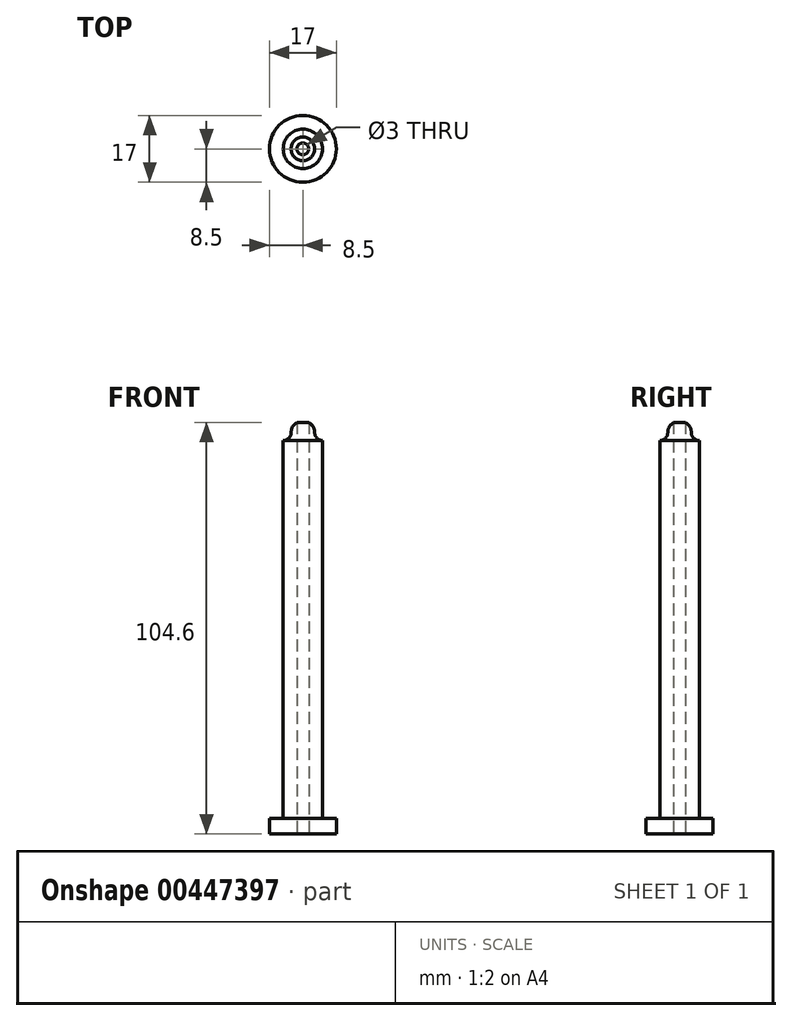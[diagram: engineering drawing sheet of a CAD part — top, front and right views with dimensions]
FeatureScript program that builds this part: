
annotation { "Feature Type Name" : "Feature", "Feature Type Description" : "" }
export const myFeature = defineFeature(function(context is Context, id is Id, definition is map)
    precondition{}
    {
        {
            var Q0;
            Q0=qCreatedBy(makeId("Top.planeOp"),FACE);
            var sketch = newSketch(context, id + "F0", { "sketchPlane" : qUnion([Q0])});
            skCircle(sketch, "E0", {"center": v(0, 0) * mm, "radius": 8.5 * mm});
            skSolve(sketch);
        }
        {
            var Q0;
            Q0=qSketchRegion(id+"F0",true);
            extrude(context, id + "F1", {"entities" : qUnion([Q0]), "depth" : 4 * mm});
        }
        {
            var Q0;
            Q0=qCreatedBy(makeId("Top.planeOp"),FACE);
            var sketch = newSketch(context, id + "F2", { "sketchPlane" : qUnion([Q0])});
            skCircle(sketch, "E1", {"center": v(0, 0) * mm, "radius": 5 * mm});
            skSolve(sketch);
        }
        {
            var Q0;
            Q0=qSketchRegion(id+"F2",true);
            extrude(context, id + "F3", {"entities" : qUnion([Q0]), "operationType" : NewBodyOperationType.ADD, "depth" : 100 * mm});
        }
        {
            var Q0;
            Q0=qCreatedBy(makeId("Right.planeOp"),FACE);
            var sketch = newSketch(context, id + "F4", { "sketchPlane" : qUnion([Q0])});
            skLineSegment(sketch, "E2", {"start": v(0, 102) * mm, "end": v(0, 100) * mm});
            skLineSegment(sketch, "E3", {"start": v(0, 100) * mm, "end": v(5, 100) * mm});
            skLineSegment(sketch, "E4", {"start": v(3, 102) * mm, "end": v(0, 102) * mm});
            skArc(sketch, "E5", {"start": v(3, 102) * mm, "mid": v(3.59, 100.59) * mm, "end": v(5, 100) * mm});
            skSolve(sketch);
        }
        {
            var Q0;
            Q0=makeQuery(id+"F4.imprint","IMPRINT",FACE,{"disambiguationData":[TD([[makeQuery(id+"F4.imprint","IMPRINT",EDGE,{"derivedFrom":sQuery(id+"F4.wireOp",EDGE,"E2")}),1.0]])]});
            var Q1;
            Q1=sQuery(id+"F4.wireOp",EDGE,"E2");
            revolve(context, id + "F5", {"operationType" : NewBodyOperationType.ADD, "entities" : qUnion([Q0]), "axis" : qUnion([Q1]), "revolveType" : RevolveType.FULL});
        }
        {
            var Q0;
            Q0=qCreatedBy(makeId("Right.planeOp"),FACE);
            var sketch = newSketch(context, id + "F6", { "sketchPlane" : qUnion([Q0])});
            skLineSegment(sketch, "E6", {"start": v(0, 102) * mm, "end": v(0, 105) * mm});
            skLineSegment(sketch, "E7", {"start": v(3, 102) * mm, "end": v(0, 102) * mm});
            skArc(sketch, "E8", {"start": v(3, 102) * mm, "mid": v(2.12, 104.12) * mm, "end": v(0, 105) * mm});
            skSolve(sketch);
        }
        {
            var Q0;
            Q0=makeQuery(id+"F6.imprint","IMPRINT",FACE,{"disambiguationData":[TD([[makeQuery(id+"F6.imprint","IMPRINT",EDGE,{"derivedFrom":sQuery(id+"F6.wireOp",EDGE,"E6")}),-1.0]])]});
            var Q1;
            Q1=sQuery(id+"F6.wireOp",EDGE,"E6");
            revolve(context, id + "F7", {"operationType" : NewBodyOperationType.ADD, "entities" : qUnion([Q0]), "axis" : qUnion([Q1]), "revolveType" : RevolveType.FULL});
        }
        {
            var Q0;
            Q0=qCreatedBy(makeId("Top.planeOp"),FACE);
            var sketch = newSketch(context, id + "F8", { "sketchPlane" : qUnion([Q0])});
            skCircle(sketch, "E9", {"center": v(0, 0) * mm, "radius": 1.5 * mm});
            skSolve(sketch);
        }
        {
            var Q0;
            Q0 = qSketchRegion(id + "F8", true);
            extrude(context, id + "F9", {"entities" : qUnion([Q0]), "operationType" : NewBodyOperationType.REMOVE, "depth" : 109.5 * mm});
        }
    });
